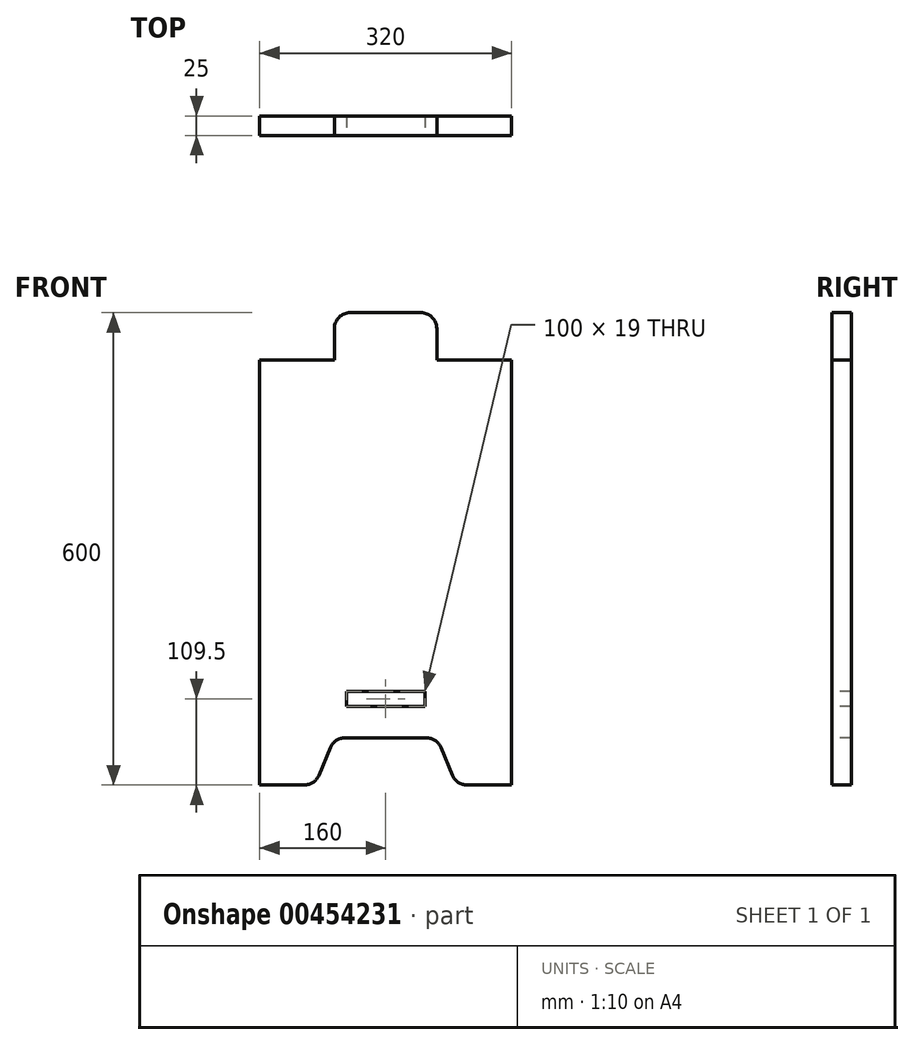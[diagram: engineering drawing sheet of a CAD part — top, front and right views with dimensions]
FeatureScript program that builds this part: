
annotation { "Feature Type Name" : "Feature", "Feature Type Description" : "" }
export const myFeature = defineFeature(function(context is Context, id is Id, definition is map)
    precondition{}
    {
        {
            var Q0;
            Q0=qCreatedBy(makeId("Front.planeOp"),FACE);
            var sketch = newSketch(context, id + "F0", { "sketchPlane" : qUnion([Q0])});
            skLineSegment(sketch, "E0.bottom", {"start": v(-160, -300) * mm, "end": v(160, -300) * mm});
            skLineSegment(sketch, "E0.top", {"start": v(-160, 300) * mm, "end": v(160, 300) * mm});
            skLineSegment(sketch, "E0.left", {"start": v(-160, -300) * mm, "end": v(-160, 300) * mm});
            skLineSegment(sketch, "E0.right", {"start": v(160, -300) * mm, "end": v(160, 300) * mm});
            skPoint(sketch, "E0.middle", {"position": v(0, 0) * mm});
            skSolve(sketch);
        }
        {
            var Q0;
            Q0=qSketchRegion(id+"F0",true);
            extrude(context, id + "F1", {"entities" : qUnion([Q0]), "depth" : 25 * mm});
        }
        {
            var Q0;
            Q0=makeQuery(id+"F1.opExtrude","CAP_FACE",FACE,{"disambiguationData":[OSD([sQuery(id+"F0.wireOp",EDGE,"E0.bottom"),sQuery(id+"F0.wireOp",EDGE,"E0.top"),sQuery(id+"F0.wireOp",EDGE,"E0.left"),sQuery(id+"F0.wireOp",EDGE,"E0.right")])],"isStart":false});
            var sketch = newSketch(context, id + "F2", { "sketchPlane" : qUnion([Q0])});
            skLineSegment(sketch, "E1", {"start": v(-84.87, -287.7) * mm, "end": v(-70.13, -252.3) * mm});
            skLineSegment(sketch, "E2", {"start": v(-51.67, -240) * mm, "end": v(51.67, -240) * mm});
            skLineSegment(sketch, "E3", {"start": v(70.13, -252.3) * mm, "end": v(84.87, -287.7) * mm});
            skLineSegment(sketch, "E4", {"start": v(103.33, -300) * mm, "end": v(160, -300) * mm});
            skLineSegment(sketch, "E5", {"start": v(-103.33, -300) * mm, "end": v(-160, -300) * mm});
            skPoint(sketch, "E6.visualSharp", {"position": v(-90, -300) * mm});
            skArc(sketch, "E6.filletArc", {"start": v(-103.33, -300) * mm, "mid": v(-92.24, -296.64) * mm, "end": v(-84.87, -287.7) * mm});
            skPoint(sketch, "E7.visualSharp", {"position": v(90, -300) * mm});
            skArc(sketch, "E7.filletArc", {"start": v(84.87, -287.7) * mm, "mid": v(92.24, -296.64) * mm, "end": v(103.33, -300) * mm});
            skPoint(sketch, "E8.visualSharp", {"position": v(-65, -240) * mm});
            skArc(sketch, "E8.filletArc", {"start": v(-51.67, -240) * mm, "mid": v(-62.76, -243.36) * mm, "end": v(-70.13, -252.3) * mm});
            skPoint(sketch, "E9.visualSharp", {"position": v(65, -240) * mm});
            skArc(sketch, "E9.filletArc", {"start": v(70.13, -252.3) * mm, "mid": v(62.76, -243.36) * mm, "end": v(51.67, -240) * mm});
            skLineSegment(sketch, "E10", {"start": v(-65, 280) * mm, "end": v(-65, 260) * mm});
            skLineSegment(sketch, "E11", {"start": v(-85, 240) * mm, "end": v(-160, 240) * mm});
            skLineSegment(sketch, "E12", {"start": v(65, 280) * mm, "end": v(65, 260) * mm});
            skLineSegment(sketch, "E13", {"start": v(85, 240) * mm, "end": v(160, 240) * mm});
            skPoint(sketch, "E14.visualSharp", {"position": v(-65, 240) * mm});
            skPoint(sketch, "E15.visualSharp", {"position": v(65, 240) * mm});
            skLineSegment(sketch, "E16", {"start": v(-45, 300) * mm, "end": v(45, 300) * mm});
            skPoint(sketch, "E17.visualSharp", {"position": v(-65, 300) * mm});
            skArc(sketch, "E17.filletArc", {"start": v(-45, 300) * mm, "mid": v(-59.14, 294.14) * mm, "end": v(-65, 280) * mm});
            skPoint(sketch, "E18.visualSharp", {"position": v(65, 300) * mm});
            skArc(sketch, "E18.filletArc", {"start": v(65, 280) * mm, "mid": v(59.14, 294.14) * mm, "end": v(45, 300) * mm});
            skLineSegment(sketch, "E19.bottom", {"start": v(-50, -181) * mm, "end": v(50, -181) * mm});
            skLineSegment(sketch, "E19.top", {"start": v(-50, -200) * mm, "end": v(50, -200) * mm});
            skLineSegment(sketch, "E19.left", {"start": v(-50, -181) * mm, "end": v(-50, -200) * mm});
            skLineSegment(sketch, "E19.right", {"start": v(50, -181) * mm, "end": v(50, -200) * mm});
            skLineSegment(sketch, "E20", {"start": v(0, 0) * mm, "end": v(0, -181) * mm, "construction": true});
            skLineSegment(sketch, "E21", {"start": v(-103.33, -300) * mm, "end": v(103.33, -300) * mm});
            skLineSegment(sketch, "E22", {"start": v(160, 240) * mm, "end": v(160, 300) * mm});
            skLineSegment(sketch, "E23", {"start": v(160, 300) * mm, "end": v(45, 300) * mm});
            skLineSegment(sketch, "E24", {"start": v(-160, 240) * mm, "end": v(-160, 300) * mm});
            skLineSegment(sketch, "E25", {"start": v(-160, 300) * mm, "end": v(-45, 300) * mm});
            skLineSegment(sketch, "E26.bottom", {"start": v(-130, 240) * mm, "end": v(-112, 240) * mm});
            skLineSegment(sketch, "E26.top", {"start": v(-130, 210) * mm, "end": v(-112, 210) * mm});
            skLineSegment(sketch, "E26.left", {"start": v(-130, 240) * mm, "end": v(-130, 210) * mm});
            skLineSegment(sketch, "E26.right", {"start": v(-112, 240) * mm, "end": v(-112, 210) * mm});
            skLineSegment(sketch, "E27.bottom", {"start": v(112, 240) * mm, "end": v(130, 240) * mm});
            skLineSegment(sketch, "E27.top", {"start": v(112, 210) * mm, "end": v(130, 210) * mm});
            skLineSegment(sketch, "E27.left", {"start": v(112, 240) * mm, "end": v(112, 210) * mm});
            skLineSegment(sketch, "E27.right", {"start": v(130, 240) * mm, "end": v(130, 210) * mm});
            skLineSegment(sketch, "E28", {"start": v(85, 240) * mm, "end": v(65, 240) * mm});
            skLineSegment(sketch, "E29", {"start": v(65, 260) * mm, "end": v(65, 240) * mm});
            skLineSegment(sketch, "E30", {"start": v(-65, 260) * mm, "end": v(-65, 240) * mm});
            skLineSegment(sketch, "E31", {"start": v(-85, 240) * mm, "end": v(-65, 240) * mm});
            skSolve(sketch);
        }
        {
            var Q0;
            Q0=makeQuery(id+"F2.imprint","IMPRINT",FACE,{"disambiguationData":[TD([[makeQuery(id+"F2.imprint","IMPRINT",EDGE,{"derivedFrom":sQuery(id+"F2.wireOp",EDGE,"E10")}),-1.0]])]});
            var Q1;
            Q1=makeQuery(id+"F2.imprint","IMPRINT",FACE,{"disambiguationData":[TD([[makeQuery(id+"F2.imprint","IMPRINT",EDGE,{"derivedFrom":sQuery(id+"F2.wireOp",EDGE,"E12")}),1.0]])]});
            var Q2;
            Q2=makeQuery(id+"F2.imprint","IMPRINT",FACE,{"disambiguationData":[TD([[makeQuery(id+"F2.imprint","IMPRINT",EDGE,{"derivedFrom":sQuery(id+"F2.wireOp",EDGE,"E1")}),-1.0]])]});
            var Q3;
            Q3=makeQuery(id+"F2.imprint","IMPRINT",FACE,{"disambiguationData":[TD([[makeQuery(id+"F2.imprint","IMPRINT",EDGE,{"derivedFrom":sQuery(id+"F2.wireOp",EDGE,"E19.bottom")}),-1.0]])]});
            var Q4;
            Q4=makeQuery(id+"F2.imprint","IMPRINT",FACE,{"disambiguationData":[TD([[makeQuery(id+"F2.imprint","IMPRINT",EDGE,{"derivedFrom":sQuery(id+"F2.wireOp",EDGE,"E26.bottom")}),-1.0]])]});
            var Q5;
            Q5=makeQuery(id+"F2.imprint","IMPRINT",FACE,{"disambiguationData":[TD([[makeQuery(id+"F2.imprint","IMPRINT",EDGE,{"derivedFrom":sQuery(id+"F2.wireOp",EDGE,"E27.bottom")}),-1.0]])]});
            var Q6;
            Q6=makeQuery(id+"F1.opExtrude","CAP_FACE",FACE,{"disambiguationData":[OSD([sQuery(id+"F0.wireOp",EDGE,"E0.bottom"),sQuery(id+"F0.wireOp",EDGE,"E0.top"),sQuery(id+"F0.wireOp",EDGE,"E0.left"),sQuery(id+"F0.wireOp",EDGE,"E0.right")])],"isStart":true});
            extrude(context, id + "F3", {"entities" : qUnion([Q0, Q1, Q2, Q3, Q4, Q5]), "operationType" : NewBodyOperationType.REMOVE, "endBound" : BoundingType.UP_TO_SURFACE, "oppositeDirection" : true, "endBoundEntityFace" : qUnion([Q6]), "depth" : 25 * mm});
        }
    });
